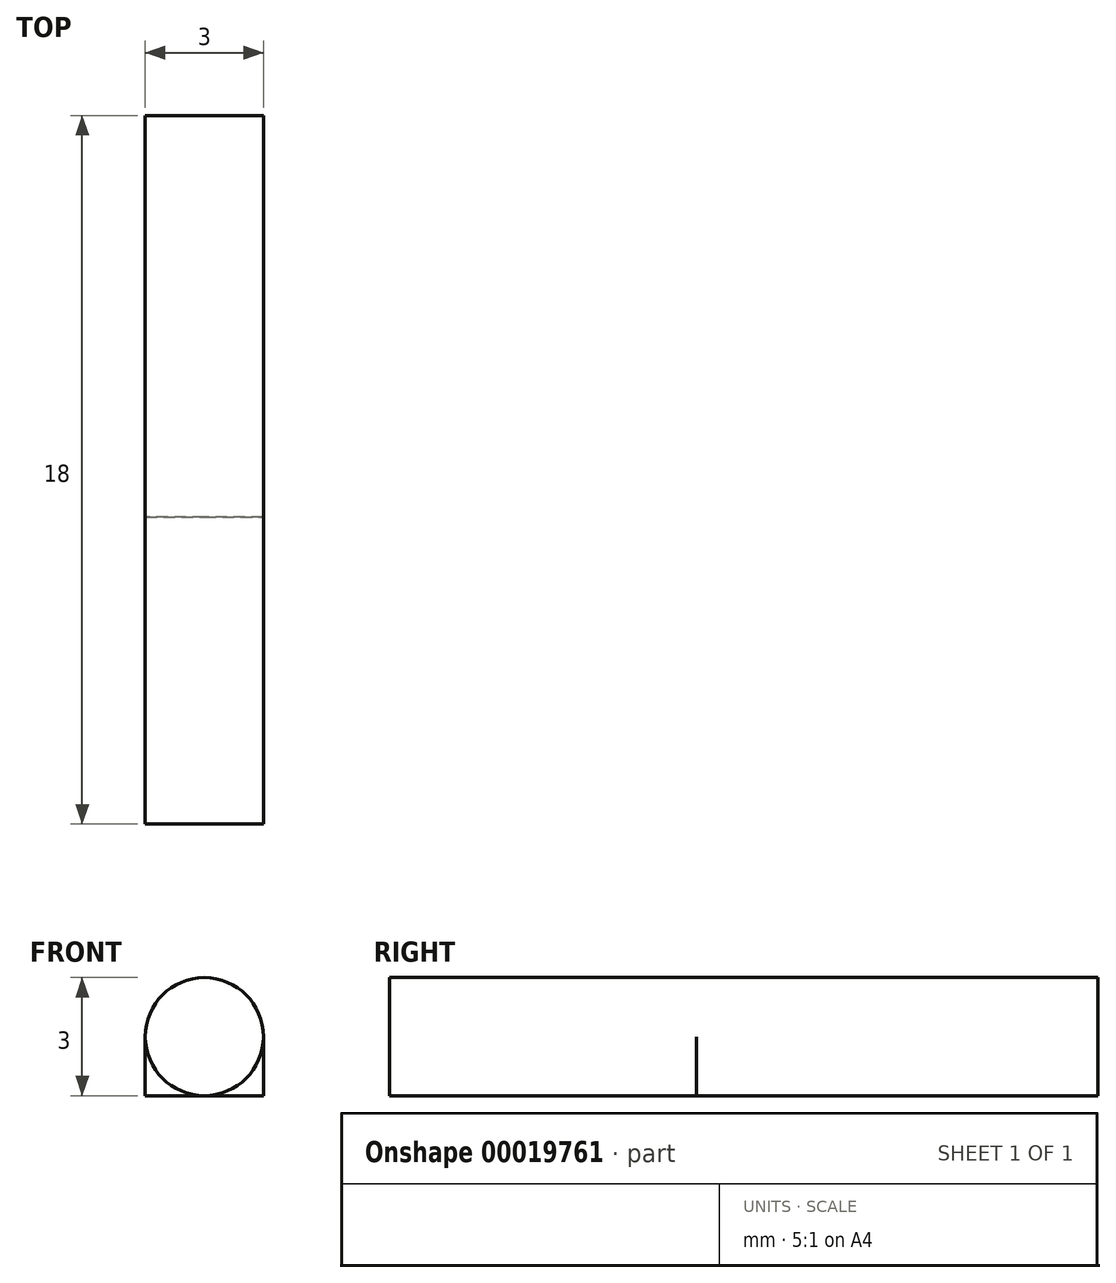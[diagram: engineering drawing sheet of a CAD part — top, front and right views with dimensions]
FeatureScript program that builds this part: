
annotation { "Feature Type Name" : "Feature", "Feature Type Description" : "" }
export const myFeature = defineFeature(function(context is Context, id is Id, definition is map)
    precondition{}
    {
        {
            var Q0;
            Q0=qCreatedBy(makeId("Front.planeOp"),FACE);
            var sketch = newSketch(context, id + "F0", { "sketchPlane" : qUnion([Q0])});
            skCircle(sketch, "E0", {"center": v(0, 0) * mm, "radius": 1.5 * mm});
            skLineSegment(sketch, "E1", {"start": v(0, 14.26) * mm, "end": v(0, -11.72) * mm, "construction": true});
            skLineSegment(sketch, "E2.rect.top", {"start": v(1.5, -1.5) * mm, "end": v(-1.5, -1.5) * mm});
            skPoint(sketch, "E2.rect.middle", {"position": v(0, -1.5) * mm});
            skLineSegment(sketch, "E3", {"start": v(-1.5, 0) * mm, "end": v(-1.5, -1.5) * mm});
            skLineSegment(sketch, "E4", {"start": v(1.5, 0) * mm, "end": v(1.5, -1.5) * mm});
            skSolve(sketch);
        }
        {
            var Q0;
            {var subQ0=sQuery(id+"F0.wireOp",EDGE,"E0");var subQ3=makeQuery(id+"F0.imprint","INTERSECT",VERTEX,{"derivedFrom":[subQ0,sQuery(id+"F0.wireOp",EDGE,"E3")]});Q0=makeQuery(id+"F0.imprint","IMPRINT",FACE,{"disambiguationData":[TD([[makeQuery(id+"F0.imprint","IMPRINT",EDGE,{"disambiguationData":[TD([[subQ3,1.0]])],"derivedFrom":subQ0}),1.0]])]});}
            extrude(context, id + "F1", {"entities" : qUnion([Q0]), "depth" : 18 * mm});
        }
        {
            var Q0;
            {var subQ0=sQuery(id+"F0.wireOp",EDGE,"E3");Q0=makeQuery(id+"F0.imprint","IMPRINT",FACE,{"disambiguationData":[TD([[makeQuery(id+"F0.imprint","IMPRINT",EDGE,{"derivedFrom":subQ0}),1.0]])]});}
            var Q1;
            {var subQ0=sQuery(id+"F0.wireOp",EDGE,"E4");Q1=makeQuery(id+"F0.imprint","IMPRINT",FACE,{"disambiguationData":[TD([[makeQuery(id+"F0.imprint","IMPRINT",EDGE,{"derivedFrom":subQ0}),-1.0]])]});}
            extrude(context, id + "F2", {"entities" : qUnion([Q0, Q1]), "operationType" : NewBodyOperationType.ADD, "depth" : 10.2 * mm});
        }
    });
